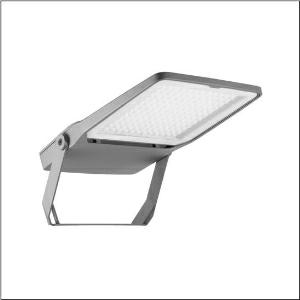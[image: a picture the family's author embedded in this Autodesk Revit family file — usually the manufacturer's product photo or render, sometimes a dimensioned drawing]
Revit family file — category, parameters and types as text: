
# Revit family: floodlight_fl_20_midi___pl52_5xa7681e2d1ac_ecaa
name_source: partatom
category: Lighting Fixtures
units: mm (PartAtom-declared; Revit-internal decimal feet)

## family parameters
Cut with Voids When Loaded = No
Host = Face
Light Source = No
Part Type = Normal
Room Calculation Point = No
Round Connector Dimension = Use Diameter
Shared = No

## types (1)
- Floodlight FL 20 midi  PL52 (1 x LED 4000K / CRI = 70 (unbekannt), 26840 lm, 4000K)
    Apparent Load = 208 VA
    CIE Flux Codes = 27 59 98 100 100
    Color Rendering = 70
    Color Temperature = 4000K
    Default Elevation = 1800 mm
    Description = Floodlight FL 20 midi, floodlight, primary light control with lens, of plastic, primary optical cover: protective disc, of toughened safety glass, transparent, light distribution: PL52, light emission: direct distribution, primary light characteristic: asymmetric, installation type: surface-mounted, LED, High Power LED, rated luminous flux: 26.840lm, luminous efficacy: 129lm/W, light colour: 740, colour temperature: 4000K, control gear: ECG Basic, control: power reduction, overheat protection, electronic power reduction, with terminal, 5-pole, max. 2.5mm², mains connection: 220..240V, AC, 50/60Hz, rated input power: 208W, LED unit, of diecast aluminium, powder-coated, Siteco® metallic grey (DB 702S), corrosivity category C5 mid according to DIN EN ISO 12944, incl. 1x M20 cable gland for cable Ø 6.5..12mm, length: 654mm, width: 450mm, height: 76mm, housing frame, of diecast aluminium, powder-coated, Siteco® metallic grey (DB 702S), mounting bracket, of steel, powder-coated, Siteco® metallic grey (DB 702S), ON/OFF, protection rating (complete): IP66, insulation class (complete): insulation class I (protective earthing), certification: CE, ENEC, VDE, protection symbol: D, permissible operating ambient temperature: -40..+40°C, permissible operating ambient temperature for outdoor applications: -40..+50°C, standard: DIN EN 12944, packaging unit: 1 piece

Light Distribution: PL52
    Height = 76 mm
    Lamp = 1 x LED 4000K / CRI >= 70 (unbekannt)
    Lamp Light Flux = 26840 lm
    Lamp count = 1
    Length = 672 mm
    Luminous efficacy = 129 lm/W
    Manufacturer = Siteco
    ModVariant = No
    Model = 5XA7681E2D1AC
    Mounting Place = Wall
    Mounting Type = Surface mounted
    Number of Poles = 1
    OnlyDefault = Yes
    Power Factor = 1
    Product Name = Floodlight FL 20 midi | PL52
    Product group = floodlight | wall mounted
    ProductGroupID = 2001
    Protection Class = Protection class I
    Protection Degree = IP 66
    RLX_Detail_Level = 1
    RLX_Emergency_Light_Flux = 0 lm
    RLX_Emergency_Type = 0
    RLX_Emergency_Type_DB = No
    RlxData = <blob elided: 94345 chars, md5=162e3a9a>
    Socket = socket
    Standby Power = 0 W
    System Light Flux = 26840 lm
    System Power = 208 W
    Type Comments = Product without accessories
    Type Image = l_1005943.jpg
    URL = http://relux.com
    VarID = ---
    Voltage = 0 V
    Weight = 0.00 kg
    Width = 450 mm

## geometry (parser evidence)
native form markers: Blend x4, Sweep x15
no freeform markers — native parametric forms only
